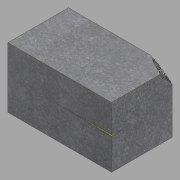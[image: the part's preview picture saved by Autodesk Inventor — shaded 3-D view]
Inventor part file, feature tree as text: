
AUTODESK INVENTOR PART (.ipt)
format: ipt  version: 2022.1 (Build 261234020, 234B)  size: 515,072 bytes
history: native  units: in
note: dims shown in document units (in); Inventor stores cm internally (conversion verified against a paired STEP export)
features: sketch x12, extrude x6, plane x4, loft x2
ambient origin geometry x8: Origin, YZ Plane, XZ Plane, XY Plane, X Axis, Y Axis, Z Axis, Center Point
bodies: Solid1 (feature_tree)
feature tree (24):
  extrude  "Extrusion1"  Depth=60.0in
  loft  "Loft1"
  sketch  "Sketch7"  dims[d79=0.0in d80=90.0deg d81=0.0in d82=0.0in]
  sketch  "Sketch8"  dims[d83=0.0in d84=0.0in d85=97.795in d86=0.0in]
  loft  "Loft2"
  sketch  "Sketch10"
  plane  "Work Plane1"
  plane  "Work Plane3"
  extrude  "Extrusion2"  TaperAngle=0.0deg  [1 undecoded]
  plane  "Work Plane4"
  extrude  "Extrusion3"  Depth=97.795in TaperAngle=0.0deg
  plane  "Work Plane5"
  extrude  "Extrusion4"  Depth=1.5in
  extrude  "Extrusion5"  [1 undecoded]
  extrude  "Extrusion6"  [1 undecoded]
  sketch  "Sketch1"  dims[d0=60.0in d1=35.0in]
  sketch  "Sketch5"  dims[d2=35.0in d3=0.0in d73=0.0in d74=90.0deg]
  sketch  "Sketch6"  dims[d75=0.0in d76=90.0deg d77=0.0in d78=90.0deg]
  sketch  "Sketch9"  dims[d87=0.25in d88=-0.2749in d89=1.5in d90=-0.0344in]
  sketch  "Sketch11"
  sketch  "Sketch12"
  sketch  "Sketch13"
  sketch  "Sketch14"
  sketch  "Sketch15"
note: 3 required parameter values undecoded (feature->parameter linkage not recoverable at this tier; creation-order binding heuristic only, values carry confidence <= 0.55)
